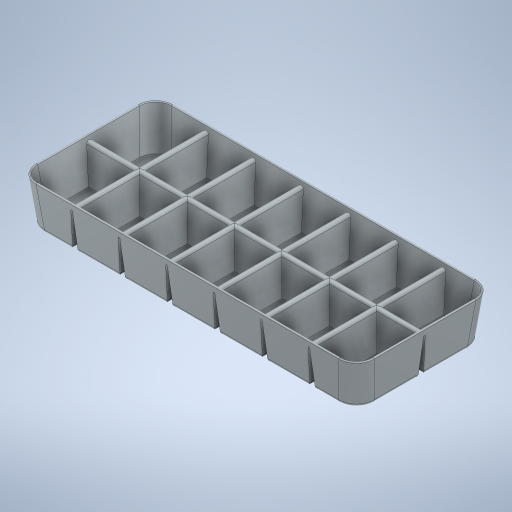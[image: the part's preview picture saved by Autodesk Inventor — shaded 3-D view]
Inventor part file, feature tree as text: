
AUTODESK INVENTOR PART (.ipt)
format: ipt  version: 2024 (Build 280153000, 153)  size: 616,960 bytes
history: native  units: mm
features: fillet x4, extrude x3, sketch x3, other x1, pattern_linear x1, shell x1, projected_geometry x1
ambient origin geometry x8: Origin, YZ Plane, XZ Plane, XY Plane, X Axis, Y Axis, Z Axis, Center Point
bodies: Volumenkörper1 (feature_tree)
feature tree (14):
  extrude  "Extrusion1"  Depth=80.0mm
  fillet  "Rundung4"  Radius=25.0mm
  other  "Flächenverjüngung4"
  extrude  "Extrusion2"  Depth=4.0mm
  extrude  "Extrusion3"  Depth=25.0mm TaperAngle=0.0deg
  pattern_linear  "Rechteckige Anordnung1"  Spacing1=1.047198mm  [1 undecoded]
  shell  "Wandung1"  Thickness=1.0mm
  fillet  "Rundung1"  Radius=4.0mm
  fillet  "Rundung2"  Radius=28.0mm
  fillet  "Rundung3"  Radius=10.0mm
  sketch  "Skizze1"  dims[d0=196.0mm d1=80.0mm d2=25.0mm d3=0.0mm]
  sketch  "Skizze2"  dims[d5=1.047198mm d6=4.0mm]
  projected_geometry  "Projizierte Kontur1"
  sketch  "Skizze3"  dims[d7=1.0mm d8=25.0mm d9=0.0mm d10=1.047198mm d11=1.0mm d12=4.0mm d13=28.0mm d14=10.0mm d15=0.0mm d16=60.0mm d18=28.0mm d21=1.047198mm d22=1.0mm d23=0.5mm d24=2.0mm d25=0.5mm d26=10.0mm]
note: 1 required parameter value undecoded (feature->parameter linkage not recoverable at this tier; creation-order binding heuristic only, values carry confidence <= 0.55)
